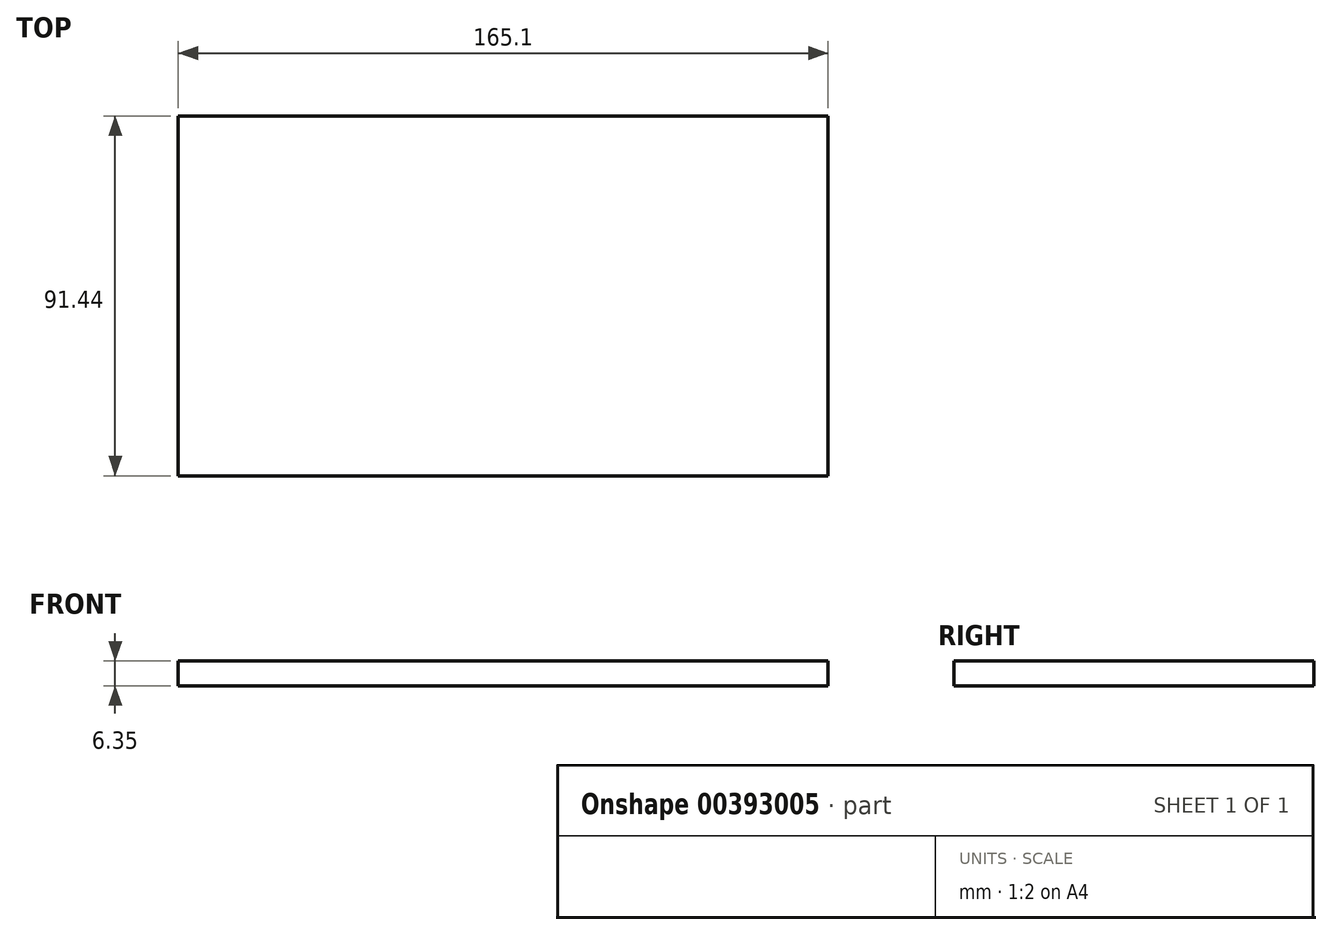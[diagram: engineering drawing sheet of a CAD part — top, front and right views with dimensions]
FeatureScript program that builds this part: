
annotation { "Feature Type Name" : "Feature", "Feature Type Description" : "" }
export const myFeature = defineFeature(function(context is Context, id is Id, definition is map)
    precondition{}
    {
        {
            var Q0;
            Q0=qCreatedBy(makeId("Top.planeOp"),FACE);
            var sketch = newSketch(context, id + "F0", { "sketchPlane" : qUnion([Q0])});
            skLineSegment(sketch, "E0.bottom", {"start": v(82.55, -45.72) * mm, "end": v(-82.55, -45.72) * mm});
            skLineSegment(sketch, "E0.top", {"start": v(82.55, 45.72) * mm, "end": v(-82.55, 45.72) * mm});
            skLineSegment(sketch, "E0.left", {"start": v(82.55, -45.72) * mm, "end": v(82.55, 45.72) * mm});
            skLineSegment(sketch, "E0.right", {"start": v(-82.55, -45.72) * mm, "end": v(-82.55, 45.72) * mm});
            skPoint(sketch, "E0.middle", {"position": v(0, 0) * mm});
            skSolve(sketch);
        }
        {
            var Q0;
            Q0 = qSketchRegion(id + "F0", true);
            extrude(context, id + "F1", {"entities" : qUnion([Q0]), "depth" : 6.35 * mm});
        }
    });
